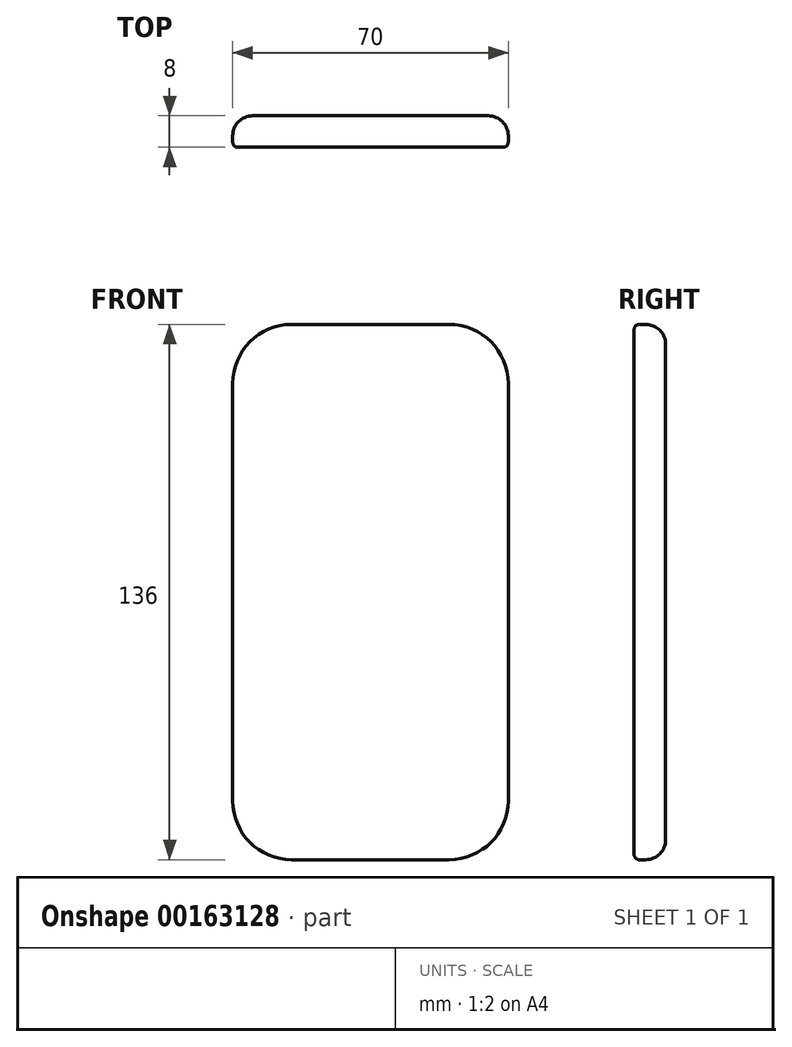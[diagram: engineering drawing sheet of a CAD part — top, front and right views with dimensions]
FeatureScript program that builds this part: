
annotation { "Feature Type Name" : "Feature", "Feature Type Description" : "" }
export const myFeature = defineFeature(function(context is Context, id is Id, definition is map)
    precondition{}
    {
        {
            var Q0;
            Q0=qCreatedBy(makeId("Front.planeOp"),FACE);
            var sketch = newSketch(context, id + "F0", { "sketchPlane" : qUnion([Q0])});
            skLineSegment(sketch, "E0.bottom", {"start": v(-35, 68) * mm, "end": v(35, 68) * mm});
            skLineSegment(sketch, "E0.top", {"start": v(-35, -68) * mm, "end": v(35, -68) * mm});
            skLineSegment(sketch, "E0.left", {"start": v(-35, 68) * mm, "end": v(-35, -68) * mm});
            skLineSegment(sketch, "E0.right", {"start": v(35, 68) * mm, "end": v(35, -68) * mm});
            skPoint(sketch, "E0.middle", {"position": v(0, 0) * mm});
            skSolve(sketch);
        }
        {
            var Q0;
            Q0 = qSketchRegion(id + "F0", true);
            extrude(context, id + "F1", {"entities" : qUnion([Q0]), "depth" : 8 * mm});
        }
        {
            var Q0;
            Q0=makeQuery(id+"F1.opExtrude","SWEPT_EDGE",EDGE,{"disambiguationData":[OSD([sQuery(id+"F0.wireOp",EDGE,"E0.bottom"),sQuery(id+"F0.wireOp",EDGE,"E0.right")])]});
            var Q1;
            Q1=makeQuery(id+"F1.opExtrude","SWEPT_EDGE",EDGE,{"disambiguationData":[OSD([sQuery(id+"F0.wireOp",EDGE,"E0.bottom"),sQuery(id+"F0.wireOp",EDGE,"E0.left")])]});
            var Q2;
            Q2=makeQuery(id+"F1.opExtrude","SWEPT_EDGE",EDGE,{"disambiguationData":[OSD([sQuery(id+"F0.wireOp",EDGE,"E0.top"),sQuery(id+"F0.wireOp",EDGE,"E0.right")])]});
            var Q3;
            Q3=makeQuery(id+"F1.opExtrude","SWEPT_EDGE",EDGE,{"disambiguationData":[OSD([sQuery(id+"F0.wireOp",EDGE,"E0.top"),sQuery(id+"F0.wireOp",EDGE,"E0.left")])]});
            fillet(context, id + "F2", {"entities" : qUnion([Q0, Q1, Q2, Q3]), "radius" : 15 * mm, "tangentPropagation" : true, "allowEdgeOverflow" : false});
        }
        {
            var Q0;
            Q0=makeQuery(id+"F1.opExtrude","CAP_EDGE",EDGE,{"disambiguationData":[OSD([sQuery(id+"F0.wireOp",EDGE,"E0.bottom")])],"isStart":true});
            var Q1;
            {var subQ0=sQuery(id+"F0.wireOp",EDGE,"E0.right");var subQ1=sQuery(id+"F0.wireOp",EDGE,"E0.bottom");Q1=makeQuery(id+"F2.opFillet","BLEND_EDGE",EDGE,{"blendedFrom":[makeQuery(id+"F1.opExtrude","SWEPT_EDGE",EDGE,{"disambiguationData":[OSD([subQ1,subQ0])]}),makeQuery(id+"F1.opExtrude","CAP_FACE",FACE,{"disambiguationData":[OSD([subQ1,sQuery(id+"F0.wireOp",EDGE,"E0.top"),sQuery(id+"F0.wireOp",EDGE,"E0.left"),subQ0])],"isStart":true})],"blendedInto":[makeQuery(id+"F1.opExtrude","CAP_FACE",FACE,{"disambiguationData":[OSD([subQ1,sQuery(id+"F0.wireOp",EDGE,"E0.top"),sQuery(id+"F0.wireOp",EDGE,"E0.left"),subQ0])],"isStart":true})]});}
            fillet(context, id + "F3", {"entities" : qUnion([Q0, Q1]), "radius" : 5.08 * mm, "tangentPropagation" : true, "allowEdgeOverflow" : false});
        }
        {
            var Q0;
            {var subQ0=sQuery(id+"F0.wireOp",EDGE,"E0.left");var subQ1=sQuery(id+"F0.wireOp",EDGE,"E0.bottom");Q0=makeQuery(id+"F2.opFillet","BLEND_EDGE",EDGE,{"blendedFrom":[makeQuery(id+"F1.opExtrude","SWEPT_EDGE",EDGE,{"disambiguationData":[OSD([subQ1,subQ0])]}),makeQuery(id+"F1.opExtrude","CAP_FACE",FACE,{"disambiguationData":[OSD([subQ1,sQuery(id+"F0.wireOp",EDGE,"E0.top"),subQ0,sQuery(id+"F0.wireOp",EDGE,"E0.right")])],"isStart":false})],"blendedInto":[makeQuery(id+"F1.opExtrude","CAP_FACE",FACE,{"disambiguationData":[OSD([subQ1,sQuery(id+"F0.wireOp",EDGE,"E0.top"),subQ0,sQuery(id+"F0.wireOp",EDGE,"E0.right")])],"isStart":false})]});}
            var Q1;
            Q1=makeQuery(id+"F1.opExtrude","CAP_EDGE",EDGE,{"disambiguationData":[OSD([sQuery(id+"F0.wireOp",EDGE,"E0.bottom")])],"isStart":false});
            fillet(context, id + "F4", {"entities" : qUnion([Q0, Q1]), "radius" : 1.27 * mm, "tangentPropagation" : true, "allowEdgeOverflow" : false});
        }
    });
